# Revit family: Accessory-Colander-KOHLER-K-37917-1
name_source: partatom
category: Specialty Equipment
units: mm (PartAtom-declared; Revit-internal decimal feet)

## family parameters
Cut with Voids When Loaded = No
Host = Face
Maintain Annotation Orientation = No
OmniClass Number = 23.31.25.00
Part Type = Normal
Room Calculation Point = No
Round Connector Dimension = Use Diameter
Shared = No

## types (4) — shared parameters
ADA Compliant = No
Assembly Code = C1030200
Date Modified = 10/14/2025
Default Elevation = 42"
Description = Colander
Finish = Kohler-Metal-NA-Stainless
Height = 4 1/4"
Length = 16 1/4"
Manufacturer = Kohler Co.
Master Format 2014 = 10 28 00
Master Format 2014 Name = Toilet, Bath, and Laundry Accessories
Material = Stainless Steel
Product Documentation Link = https://www.us.kohler.com
Product Page URL = http://www.us.kohler.com
URL = https://www.us.kohler.com
WaterSense Certified = No
Width = 6 5/8"

## per-type parameters (varying)
| type | Model | Secondary Finish | Type |
| PAP, NA-Stainless | K-37917-PAP-NA | KOHLER-Paper_Composite-PAP-Slate | 1 |
| WAL, NA-Stainless | K-37917-WAL-NA | Kohler-Wood-WAL-Walnut | 2 |
| WHK, NA-Stainless | K-37917-WHK-NA | Kohler-Wood-WHK-White_Oak | 3 |
| MPL, NA-Stainless | K-37917-MPL-NA | Kohler-Wood-1WR-Natural_Maple | 4 |

## geometry (parser evidence)
native form markers: Sweep x5
no freeform markers — native parametric forms only
